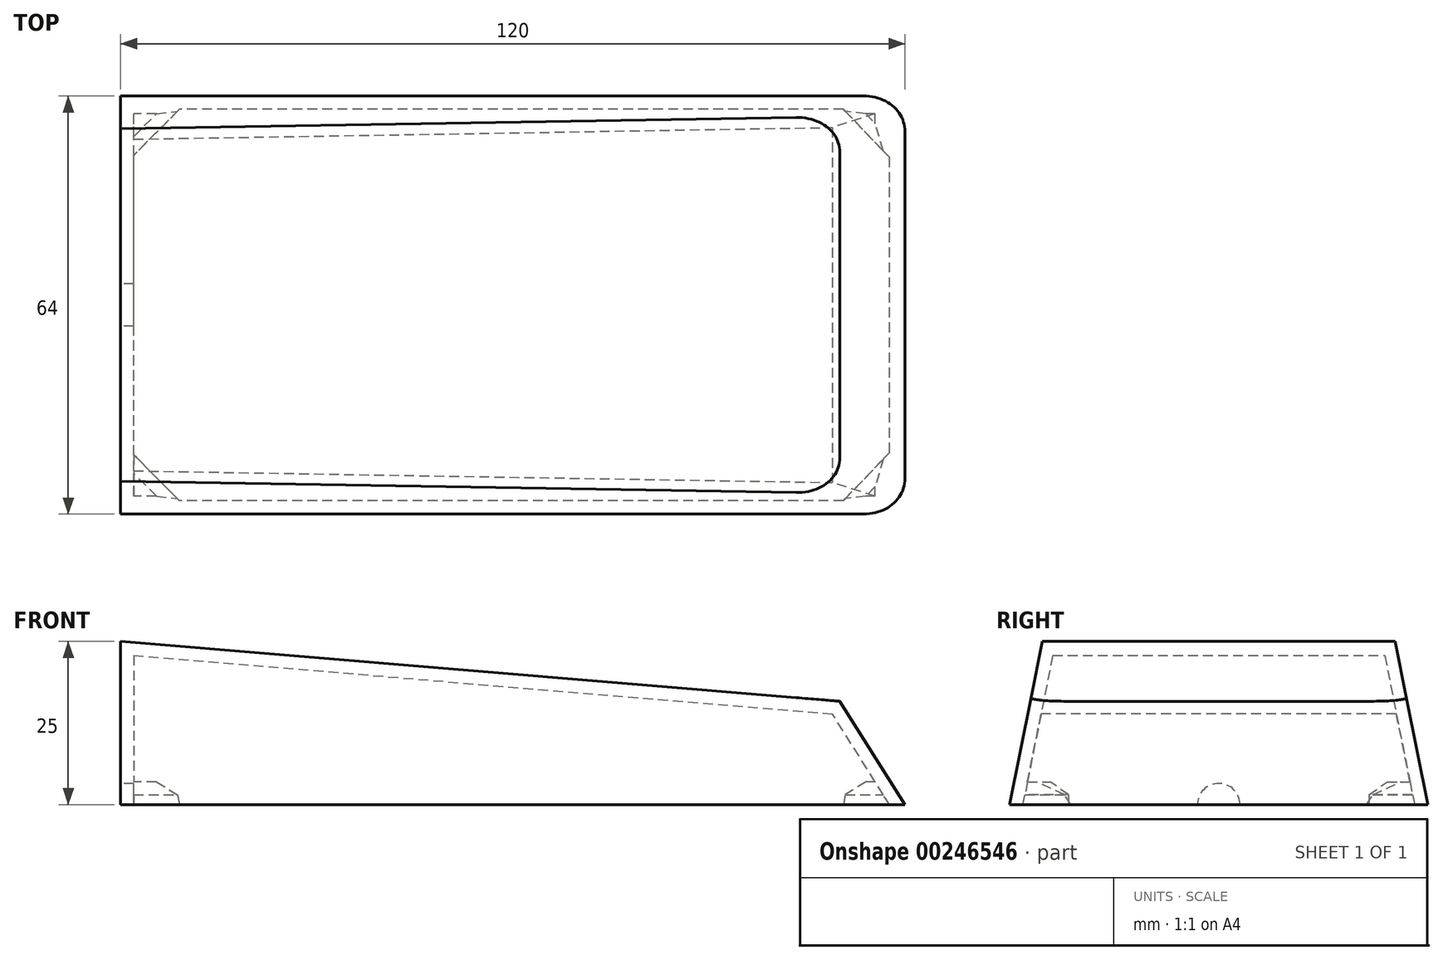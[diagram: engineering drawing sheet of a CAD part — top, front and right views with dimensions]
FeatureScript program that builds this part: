
annotation { "Feature Type Name" : "Feature", "Feature Type Description" : "" }
export const myFeature = defineFeature(function(context is Context, id is Id, definition is map)
    precondition{}
    {
        {
            var Q0;
            Q0=qCreatedBy(makeId("Top.planeOp"),FACE);
            var sketch = newSketch(context, id + "F0", { "sketchPlane" : qUnion([Q0])});
            skLineSegment(sketch, "E0.bottom", {"start": v(60, -32) * mm, "end": v(-60, -32) * mm});
            skLineSegment(sketch, "E0.top", {"start": v(60, 32) * mm, "end": v(-60, 32) * mm});
            skLineSegment(sketch, "E0.left", {"start": v(60, -32) * mm, "end": v(60, 32) * mm});
            skLineSegment(sketch, "E0.right", {"start": v(-60, -32) * mm, "end": v(-60, 32) * mm});
            skPoint(sketch, "E0.middle", {"position": v(0, 0) * mm});
            skSolve(sketch);
        }
        {
            var Q0;
            Q0=makeQuery(id+"F0.imprint","IMPRINT",FACE,{"disambiguationData":[TD([[makeQuery(id+"F0.imprint","IMPRINT",EDGE,{"derivedFrom":sQuery(id+"F0.wireOp",EDGE,"E0.bottom")}),-1.0]])]});
            extrude(context, id + "F1", {"entities" : qUnion([Q0]), "depth" : 25 * mm});
        }
        {
            var Q0;
            Q0=makeQuery(id+"F1.opExtrude","SWEPT_FACE",FACE,{"disambiguationData":[OSD([sQuery(id+"F0.wireOp",EDGE,"E0.bottom")])]});
            var sketch = newSketch(context, id + "F2", { "sketchPlane" : qUnion([Q0])});
            skLineSegment(sketch, "E1", {"start": v(-60, 25) * mm, "end": v(60, 15) * mm});
            skLineSegment(sketch, "E2", {"start": v(60, 15) * mm, "end": v(60, 25) * mm});
            skSolve(sketch);
        }
        {
            var Q0;
            Q0=makeQuery(id+"F2.imprint","IMPRINT",FACE,{"disambiguationData":[TD([[makeQuery(id+"F2.imprint","IMPRINT",EDGE,{"derivedFrom":sQuery(id+"F2.wireOp",EDGE,"E1")}),1.0]])]});
            extrude(context, id + "F3", {"entities" : qUnion([Q0]), "operationType" : NewBodyOperationType.REMOVE, "endBound" : BoundingType.THROUGH_ALL, "oppositeDirection" : true, "depth" : 25 * mm});
        }
        {
            var Q0;
            Q0=makeQuery(id+"F1.opExtrude","SWEPT_FACE",FACE,{"disambiguationData":[OSD([sQuery(id+"F0.wireOp",EDGE,"E0.bottom")])]});
            var sketch = newSketch(context, id + "F4", { "sketchPlane" : qUnion([Q0])});
            skLineSegment(sketch, "E3", {"start": v(60, 0) * mm, "end": v(50.03, 15.83) * mm});
            skLineSegment(sketch, "E4", {"start": v(50.03, 15.83) * mm, "end": v(60, 15) * mm});
            skLineSegment(sketch, "E5", {"start": v(60, 15) * mm, "end": v(71.15, 4.15) * mm});
            skLineSegment(sketch, "E6", {"start": v(71.15, 4.15) * mm, "end": v(60, 0) * mm});
            skSolve(sketch);
        }
        {
            var Q0;
            Q0=makeQuery(id+"F4.imprint","IMPRINT",FACE,{"disambiguationData":[TD([[makeQuery(id+"F4.imprint","IMPRINT",EDGE,{"derivedFrom":sQuery(id+"F4.wireOp",EDGE,"E3")}),-1.0]])]});
            extrude(context, id + "F5", {"entities" : qUnion([Q0]), "operationType" : NewBodyOperationType.REMOVE, "endBound" : BoundingType.THROUGH_ALL, "oppositeDirection" : true, "depth" : 25 * mm});
        }
        {
            var Q0;
            Q0=makeQuery(id+"F1.opExtrude","SWEPT_FACE",FACE,{"disambiguationData":[OSD([sQuery(id+"F0.wireOp",EDGE,"E0.right")])]});
            var sketch = newSketch(context, id + "F6", { "sketchPlane" : qUnion([Q0])});
            skLineSegment(sketch, "E7", {"start": v(-32, 25) * mm, "end": v(-27, 25) * mm});
            skLineSegment(sketch, "E8", {"start": v(-27, 25) * mm, "end": v(-32, 0) * mm});
            skLineSegment(sketch, "E9", {"start": v(0, 25) * mm, "end": v(0, 19.74) * mm, "construction": true});
            skPoint(sketch, "E9.endSnap0", {"position": v(0, 25) * mm});
            skLineSegment(sketch, "E10.MirrorCS", {"start": v(27, 25) * mm, "end": v(32, 0) * mm});
            skLineSegment(sketch, "E11.MirrorCS", {"start": v(32, 25) * mm, "end": v(27, 25) * mm});
            skLineSegment(sketch, "E12", {"start": v(-32, 25) * mm, "end": v(-32, 0) * mm});
            skLineSegment(sketch, "E13", {"start": v(32, 0) * mm, "end": v(32, 25) * mm});
            skSolve(sketch);
        }
        {
            var Q0;
            Q0 = qSketchRegion(id + "F6", true);
            extrude(context, id + "F7", {"entities" : qUnion([Q0]), "operationType" : NewBodyOperationType.REMOVE, "endBound" : BoundingType.THROUGH_ALL, "oppositeDirection" : true, "depth" : 25 * mm});
        }
        {
            var Q0;
            Q0=makeQuery(id+"F1.opExtrude","CAP_FACE",FACE,{"disambiguationData":[OSD([sQuery(id+"F0.wireOp",EDGE,"E0.bottom"),sQuery(id+"F0.wireOp",EDGE,"E0.top"),sQuery(id+"F0.wireOp",EDGE,"E0.left"),sQuery(id+"F0.wireOp",EDGE,"E0.right")])],"isStart":true});
            shell(context, id + "F8", {"entities" : qUnion([Q0]), "thickness" : 2 * mm});
        }
        {
            var Q0;
            Q0=makeQuery(id+"F1.opExtrude","SWEPT_FACE",FACE,{"disambiguationData":[OSD([sQuery(id+"F0.wireOp",EDGE,"E0.right")])]});
            var sketch = newSketch(context, id + "F9", { "sketchPlane" : qUnion([Q0])});
            skCircle(sketch, "E14", {"center": v(0, 0) * mm, "radius": 3.26 * mm});
            skSolve(sketch);
        }
        {
            var Q0;
            Q0 = qSketchRegion(id + "F9", true);
            extrude(context, id + "F10", {"entities" : qUnion([Q0]), "operationType" : NewBodyOperationType.REMOVE, "oppositeDirection" : true, "depth" : 25 * mm});
        }
        {
            var Q0;
            Q0=makeQuery(id+"F1.opExtrude","CAP_FACE",FACE,{"disambiguationData":[OSD([sQuery(id+"F0.wireOp",EDGE,"E0.bottom"),sQuery(id+"F0.wireOp",EDGE,"E0.top"),sQuery(id+"F0.wireOp",EDGE,"E0.left"),sQuery(id+"F0.wireOp",EDGE,"E0.right")])],"isStart":true});
            var sketch = newSketch(context, id + "F11", { "sketchPlane" : qUnion([Q0])});
            skLineSegment(sketch, "E15", {"start": v(-58, 29.96) * mm, "end": v(-51, 29.96) * mm});
            skLineSegment(sketch, "E16", {"start": v(-51, 29.96) * mm, "end": v(-58, 22.96) * mm});
            skLineSegment(sketch, "E17", {"start": v(-58, 22.96) * mm, "end": v(-58, 29.96) * mm});
            skLineSegment(sketch, "E18", {"start": v(57.64, 29.96) * mm, "end": v(50.57, 29.96) * mm});
            skLineSegment(sketch, "E19", {"start": v(50.57, 29.96) * mm, "end": v(57.64, 22.59) * mm});
            skLineSegment(sketch, "E20", {"start": v(57.64, 22.59) * mm, "end": v(57.64, 29.96) * mm});
            skLineSegment(sketch, "E21", {"start": v(57.64, 0) * mm, "end": v(48.22, 0) * mm});
            skLineSegment(sketch, "E22.MirrorCS", {"start": v(50.57, -29.96) * mm, "end": v(57.64, -22.59) * mm});
            skLineSegment(sketch, "E23.MirrorCS", {"start": v(57.64, -22.59) * mm, "end": v(57.64, -29.96) * mm});
            skLineSegment(sketch, "E24.MirrorCS", {"start": v(57.64, -29.96) * mm, "end": v(50.57, -29.96) * mm});
            skLineSegment(sketch, "E25.MirrorCS", {"start": v(-58, -29.96) * mm, "end": v(-51, -29.96) * mm});
            skLineSegment(sketch, "E26.MirrorCS", {"start": v(-58, -22.96) * mm, "end": v(-58, -29.96) * mm});
            skLineSegment(sketch, "E27.MirrorCS", {"start": v(-51, -29.96) * mm, "end": v(-58, -22.96) * mm});
            skSolve(sketch);
        }
        {
            var Q0;
            Q0 = qSketchRegion(id + "F11", true);
            extrude(context, id + "F12", {"entities" : qUnion([Q0]), "operationType" : NewBodyOperationType.ADD, "oppositeDirection" : true, "depth" : 3.5 * mm});
        }
        {
            var Q0;
            Q0=makeQuery(id+"F12.opExtrude","CAP_EDGE",EDGE,{"disambiguationData":[OSD([sQuery(id+"F11.wireOp",EDGE,"E27.MirrorCS")])],"isStart":false});
            var Q1;
            Q1=makeQuery(id+"F12.opExtrude","CAP_EDGE",EDGE,{"disambiguationData":[OSD([sQuery(id+"F11.wireOp",EDGE,"E19")])],"isStart":false});
            var Q2;
            Q2=makeQuery(id+"F12.opExtrude","CAP_EDGE",EDGE,{"disambiguationData":[OSD([sQuery(id+"F11.wireOp",EDGE,"E16")])],"isStart":false});
            var Q3;
            Q3=makeQuery(id+"F12.opExtrude","CAP_EDGE",EDGE,{"disambiguationData":[OSD([sQuery(id+"F11.wireOp",EDGE,"E22.MirrorCS")])],"isStart":false});
            chamfer(context, id + "F13", {"entities" : qUnion([Q0, Q1, Q2, Q3]), "width" : 2 * mm, "tangentPropagation" : true});
        }
        {
            var Q0;
            Q0=makeQuery(id+"F7.boolean.opBoolean","INTERSECT",EDGE,{"derivedFrom":[makeQuery(id+"F5.boolean.opBoolean","COPY",FACE,{"derivedFrom":makeQuery(id+"F5.opExtrude","SWEPT_FACE",FACE,{"disambiguationData":[OSD([sQuery(id+"F4.wireOp",EDGE,"E3")])]})}),makeQuery(id+"F7.opExtrude","SWEPT_FACE",FACE,{"disambiguationData":[OSD([sQuery(id+"F6.wireOp",EDGE,"E10.MirrorCS")])]})]});
            var Q1;
            Q1=makeQuery(id+"F7.boolean.opBoolean","INTERSECT",EDGE,{"derivedFrom":[makeQuery(id+"F5.boolean.opBoolean","COPY",FACE,{"derivedFrom":makeQuery(id+"F5.opExtrude","SWEPT_FACE",FACE,{"disambiguationData":[OSD([sQuery(id+"F4.wireOp",EDGE,"E3")])]})}),makeQuery(id+"F7.opExtrude","SWEPT_FACE",FACE,{"disambiguationData":[OSD([sQuery(id+"F6.wireOp",EDGE,"E8")])]})]});
            var Q2;
            Q2=makeQuery(id+"F7.boolean.opBoolean","COPY",EDGE,{"derivedFrom":makeQuery(id+"F7.opExtrude","CAP_EDGE",EDGE,{"disambiguationData":[OSD([sQuery(id+"F6.wireOp",EDGE,"E10.MirrorCS")])],"isStart":true})});
            var Q3;
            Q3=makeQuery(id+"F7.boolean.opBoolean","COPY",EDGE,{"derivedFrom":makeQuery(id+"F7.opExtrude","CAP_EDGE",EDGE,{"disambiguationData":[OSD([sQuery(id+"F6.wireOp",EDGE,"E8")])],"isStart":true})});
            fillet(context, id + "F14", {"entities" : qUnion([Q0, Q1, Q2, Q3]), "radius" : 6 * mm, "tangentPropagation" : true, "allowEdgeOverflow" : false});
        }
    });
